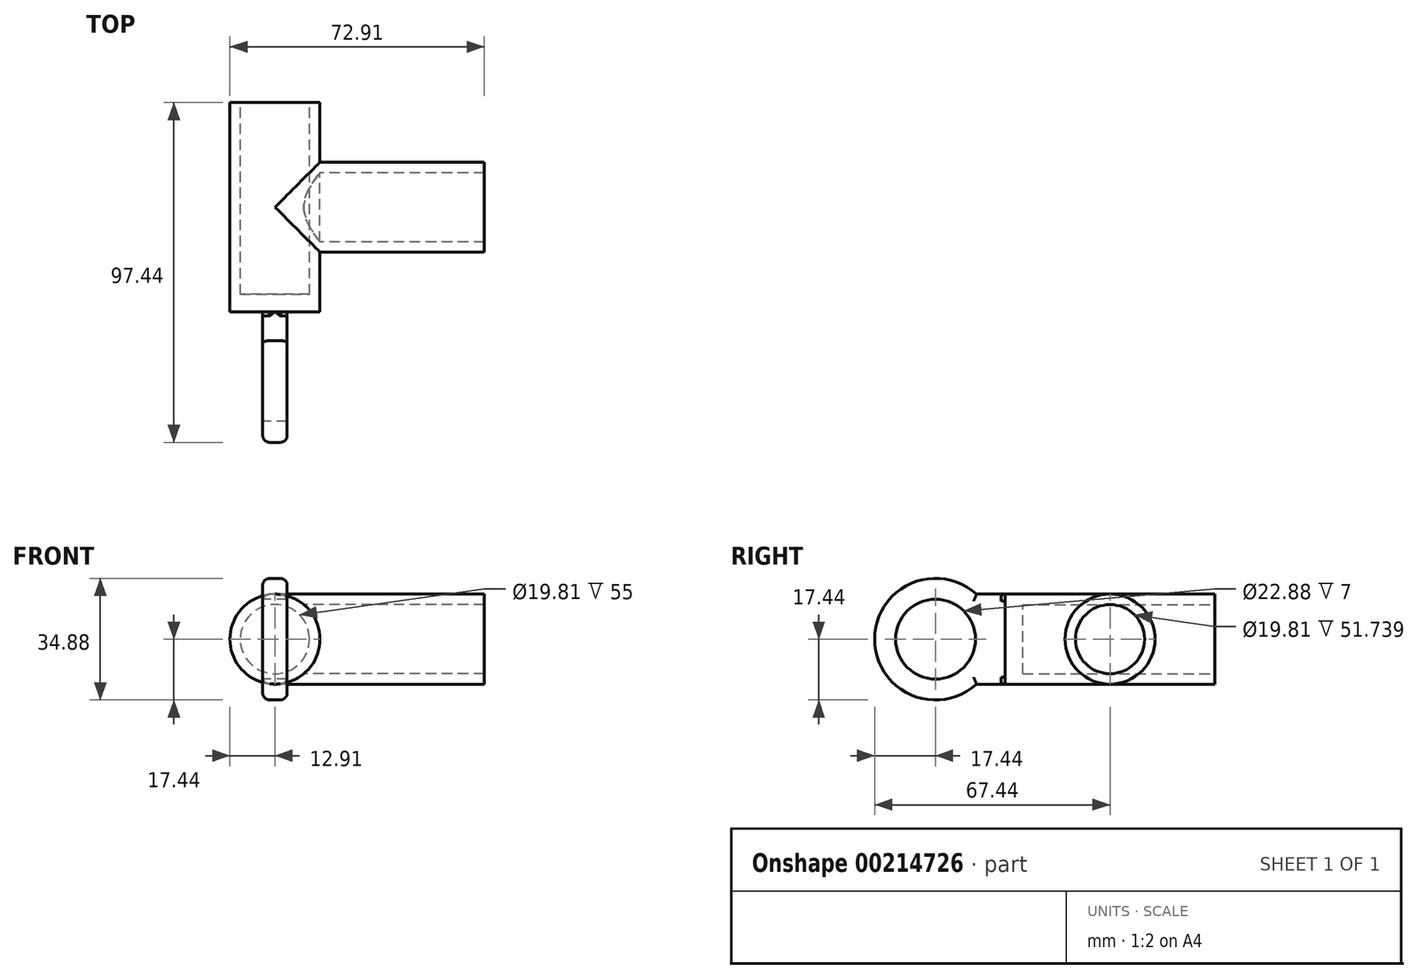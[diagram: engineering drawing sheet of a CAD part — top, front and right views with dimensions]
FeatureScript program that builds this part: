
annotation { "Feature Type Name" : "Feature", "Feature Type Description" : "" }
export const myFeature = defineFeature(function(context is Context, id is Id, definition is map)
    precondition{}
    {
        {
            assignVariable(context, id + "F0", {"name" : "ZZW", "anyValue" : 7});
        }
        {
            var Q0;
            Q0=qCreatedBy(makeId("Front.planeOp"),FACE);
            var sketch = newSketch(context, id + "F1", { "sketchPlane" : qUnion([Q0])});
            skCircle(sketch, "E0", {"center": v(0, 0) * mm, "radius": 9.9 * mm});
            skCircle(sketch, "E1", {"center": v(0, 0) * mm, "radius": 12.9 * mm});
            skSolve(sketch);
        }
        {
            var Q0;
            Q0 = qSketchRegion(id + "F1", true);
            extrude(context, id + "F2", {"entities" : qUnion([Q0]), "depth" : 55 * mm});
        }
        {
            var Q0;
            Q0=makeQuery(id+"F2.opExtrude","CAP_FACE",FACE,{"disambiguationData":[OSD([sQuery(id+"F1.wireOp",EDGE,"E0"),sQuery(id+"F1.wireOp",EDGE,"E1")])],"isStart":false});
            var sketch = newSketch(context, id + "F3", { "sketchPlane" : qUnion([Q0])});
            skCircle(sketch, "E2", {"center": v(0, 0) * mm, "radius": 12.9 * mm});
            skSolve(sketch);
        }
        {
            var Q0;
            Q0 = qSketchRegion(id + "F3", true);
            extrude(context, id + "F4", {"entities" : qUnion([Q0]), "operationType" : NewBodyOperationType.ADD, "depth" : 5 * mm});
        }
        {
            var Q0;
            Q0=qCreatedBy(makeId("Right.planeOp"),FACE);
            var sketch = newSketch(context, id + "F5", { "sketchPlane" : qUnion([Q0]), "disableImprinting" : false});
            skLineSegment(sketch, "E3", {"start": v(0, 0) * mm, "end": v(0, -12.9) * mm, "construction": true});
            skLineSegment(sketch, "E4", {"start": v(0, -12.9) * mm, "end": v(-60, -12.9) * mm, "construction": true});
            skLineSegment(sketch, "E5", {"start": v(-60, 0) * mm, "end": v(-60, 12.9) * mm, "construction": true});
            skLineSegment(sketch, "E6", {"start": v(-60, -12.9) * mm, "end": v(-80, -12.9) * mm});
            skLineSegment(sketch, "E7", {"start": v(-80, -12.9) * mm, "end": v(-80, 12.9) * mm});
            skLineSegment(sketch, "E8", {"start": v(-80, 12.9) * mm, "end": v(-60, 12.9) * mm});
            skLineSegment(sketch, "E9", {"start": v(-60, -12.9) * mm, "end": v(-60, 12.9) * mm});
            skCircle(sketch, "E10", {"center": v(-80, 0) * mm, "radius": 11.44 * mm});
            skCircle(sketch, "E11", {"center": v(-80, 0) * mm, "radius": 17.44 * mm});
            skSolve(sketch);
        }
        {
            var Q0;
            {var subQ1=sQuery(id+"F5.wireOp",EDGE,"E7");var subQ5=sQuery(id+"F5.wireOp",EDGE,"E6");var subQ6=makeQuery(id+"F5.imprint","INTERSECT",VERTEX,{"derivedFrom":[subQ5,subQ1]});Q0=makeQuery(id+"F5.imprint","IMPRINT",FACE,{"disambiguationData":[TD([[makeQuery(id+"F5.imprint","IMPRINT",EDGE,{"disambiguationData":[TD([[subQ6,1.0]])],"derivedFrom":subQ5}),1.0]])]});}
            var Q1;
            {var subQ0=sQuery(id+"F5.wireOp",EDGE,"E9");Q1=makeQuery(id+"F5.imprint","IMPRINT",FACE,{"disambiguationData":[TD([[makeQuery(id+"F5.imprint","IMPRINT",EDGE,{"derivedFrom":subQ0}),1.0]])]});}
            var Q2;
            {var subQ1=sQuery(id+"F5.wireOp",EDGE,"E7");var subQ5=sQuery(id+"F5.wireOp",EDGE,"E6");var subQ6=makeQuery(id+"F5.imprint","INTERSECT",VERTEX,{"derivedFrom":[subQ5,subQ1]});Q2=makeQuery(id+"F5.imprint","IMPRINT",FACE,{"disambiguationData":[TD([[makeQuery(id+"F5.imprint","IMPRINT",EDGE,{"disambiguationData":[TD([[subQ6,1.0]])],"derivedFrom":subQ5}),-1.0]])]});}
            extrude(context, id + "F6", {"entities" : qUnion([Q0, Q1, Q2]), "operationType" : NewBodyOperationType.ADD, "depth" : (getVariable(context, 'ZZW') / 2) * mm, "hasSecondDirection" : true, "secondDirectionOppositeDirection" : true, "secondDirectionDepth" : (getVariable(context, 'ZZW') / 2) * mm});
        }
        {
            var Q0;
            {var subQ0=sQuery(id+"F5.wireOp",EDGE,"E9");var subQ1=sQuery(id+"F5.wireOp",EDGE,"E6");Q0=makeQuery(id+"F6.boolean.opBoolean","SPLIT",EDGE,{"disambiguationData":[TD([makeQuery(id+"F6.opExtrude","CAP_FACE",FACE,{"disambiguationData":[OSD([subQ1,sQuery(id+"F5.wireOp",EDGE,"E8"),subQ0,sQuery(id+"F5.wireOp",EDGE,"E10"),sQuery(id+"F5.wireOp",EDGE,"E11")])],"isStart":true})])],"derivedFrom":makeQuery(id+"F6.opExtrude","SWEPT_EDGE",EDGE,{"disambiguationData":[OSD([subQ1,subQ0])]})});}
            var Q1;
            {var subQ0=sQuery(id+"F5.wireOp",EDGE,"E6");var subQ1=sQuery(id+"F5.wireOp",EDGE,"E9");Q1=makeQuery(id+"F6.boolean.opBoolean","SPLIT",EDGE,{"disambiguationData":[TD([makeQuery(id+"F6.opExtrude","CAP_FACE",FACE,{"disambiguationData":[OSD([subQ0,sQuery(id+"F5.wireOp",EDGE,"E8"),subQ1,sQuery(id+"F5.wireOp",EDGE,"E10"),sQuery(id+"F5.wireOp",EDGE,"E11")])],"isStart":false})])],"derivedFrom":makeQuery(id+"F6.opExtrude","SWEPT_EDGE",EDGE,{"disambiguationData":[OSD([subQ0,subQ1])]})});}
            fillet(context, id + "F7", {"entities" : qUnion([Q0, Q1]), "radius" : 5 * mm, "tangentPropagation" : true, "allowEdgeOverflow" : false});
        }
        {
            var Q0;
            {var subQ0=sQuery(id+"F5.wireOp",EDGE,"E9");var subQ1=sQuery(id+"F5.wireOp",EDGE,"E8");Q0=makeQuery(id+"F6.boolean.opBoolean","SPLIT",EDGE,{"disambiguationData":[TD([makeQuery(id+"F6.opExtrude","CAP_FACE",FACE,{"disambiguationData":[OSD([sQuery(id+"F5.wireOp",EDGE,"E6"),subQ1,subQ0,sQuery(id+"F5.wireOp",EDGE,"E10"),sQuery(id+"F5.wireOp",EDGE,"E11")])],"isStart":true})])],"derivedFrom":makeQuery(id+"F6.opExtrude","SWEPT_EDGE",EDGE,{"disambiguationData":[OSD([subQ1,subQ0])]})});}
            var Q1;
            {var subQ0=sQuery(id+"F5.wireOp",EDGE,"E9");var subQ1=sQuery(id+"F5.wireOp",EDGE,"E8");Q1=makeQuery(id+"F6.boolean.opBoolean","SPLIT",EDGE,{"disambiguationData":[TD([makeQuery(id+"F6.opExtrude","CAP_FACE",FACE,{"disambiguationData":[OSD([sQuery(id+"F5.wireOp",EDGE,"E6"),subQ1,subQ0,sQuery(id+"F5.wireOp",EDGE,"E10"),sQuery(id+"F5.wireOp",EDGE,"E11")])],"isStart":false})])],"derivedFrom":makeQuery(id+"F6.opExtrude","SWEPT_EDGE",EDGE,{"disambiguationData":[OSD([subQ1,subQ0])]})});}
            fillet(context, id + "F8", {"entities" : qUnion([Q0, Q1]), "radius" : 5 * mm, "tangentPropagation" : true, "allowEdgeOverflow" : false});
        }
        {
            var Q0;
            Q0=makeQuery(id+"F6.opExtrude","CAP_EDGE",EDGE,{"disambiguationData":[OSD([sQuery(id+"F5.wireOp",EDGE,"E11")])],"isStart":true});
            fillet(context, id + "F9", {"entities" : qUnion([Q0]), "radius" : 2 * mm, "tangentPropagation" : true, "allowEdgeOverflow" : false});
        }
        {
            var Q0;
            Q0=makeQuery(id+"F6.opExtrude","CAP_EDGE",EDGE,{"disambiguationData":[OSD([sQuery(id+"F5.wireOp",EDGE,"E11")])],"isStart":false});
            fillet(context, id + "F10", {"entities" : qUnion([Q0]), "radius" : 2 * mm, "tangentPropagation" : true, "allowEdgeOverflow" : false});
        }
        {
            var Q0;
            Q0=makeQuery(id+"F6.opExtrude","CAP_EDGE",EDGE,{"disambiguationData":[OSD([sQuery(id+"F5.wireOp",EDGE,"E6")])],"isStart":false});
            fillet(context, id + "F11", {"entities" : qUnion([Q0]), "radius" : 2 * mm, "tangentPropagation" : true, "allowEdgeOverflow" : false});
        }
        {
            var Q0;
            Q0=makeQuery(id+"F6.opExtrude","CAP_EDGE",EDGE,{"disambiguationData":[OSD([sQuery(id+"F5.wireOp",EDGE,"E6")])],"isStart":true});
            fillet(context, id + "F12", {"entities" : qUnion([Q0]), "radius" : 2 * mm, "tangentPropagation" : true, "allowEdgeOverflow" : false});
        }
        {
            var Q0;
            Q0=makeQuery(id+"F6.opExtrude","CAP_EDGE",EDGE,{"disambiguationData":[OSD([sQuery(id+"F5.wireOp",EDGE,"E8")])],"isStart":true});
            fillet(context, id + "F13", {"entities" : qUnion([Q0]), "radius" : 2 * mm, "tangentPropagation" : true, "allowEdgeOverflow" : false});
        }
        {
            var Q0;
            Q0=makeQuery(id+"F6.opExtrude","CAP_EDGE",EDGE,{"disambiguationData":[OSD([sQuery(id+"F5.wireOp",EDGE,"E8")])],"isStart":false});
            fillet(context, id + "F14", {"entities" : qUnion([Q0]), "radius" : 2 * mm, "tangentPropagation" : true, "allowEdgeOverflow" : false});
        }
        {
            var Q0;
            Q0=qCreatedBy(makeId("Right.planeOp"),FACE);
            var sketch = newSketch(context, id + "F15", { "sketchPlane" : qUnion([Q0]), "disableImprinting" : false});
            skCircle(sketch, "E12", {"center": v(-30, 0) * mm, "radius": 9.9 * mm});
            skCircle(sketch, "E13", {"center": v(-30, 0) * mm, "radius": 12.9 * mm});
            skSolve(sketch);
        }
        {
            var Q0;
            Q0 = qSketchRegion(id + "F15", true);
            extrude(context, id + "F16", {"entities" : qUnion([Q0]), "operationType" : NewBodyOperationType.ADD, "depth" : 60 * mm});
        }
        {
            var Q0;
            Q0=makeQuery(id+"F4.opExtrude","CAP_FACE",FACE,{"disambiguationData":[OSD([sQuery(id+"F3.wireOp",EDGE,"E2")])],"isStart":true});
            var sketch = newSketch(context, id + "F17", { "sketchPlane" : qUnion([Q0])});
            skCircle(sketch, "E14", {"center": v(0, 0) * mm, "radius": 9.9 * mm});
            skSolve(sketch);
        }
        {
            var Q0;
            Q0 = qSketchRegion(id + "F17", true);
            extrude(context, id + "F18", {"entities" : qUnion([Q0]), "operationType" : NewBodyOperationType.REMOVE, "depth" : 60 * mm});
        }
    });
